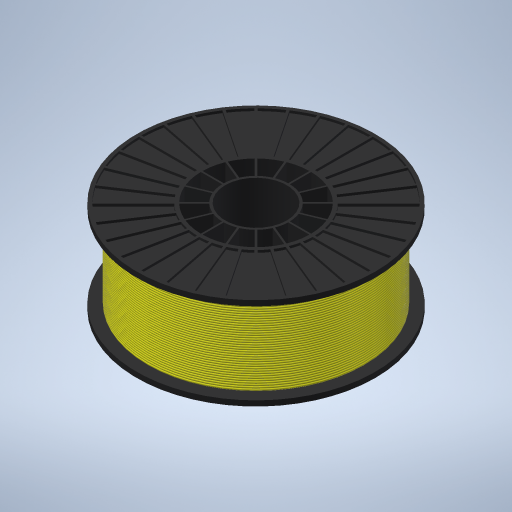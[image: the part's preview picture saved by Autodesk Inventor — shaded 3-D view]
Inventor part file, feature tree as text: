
AUTODESK INVENTOR PART (.ipt)
format: ipt  version: 2024 (Build 280153000, 153)  size: 1,131,008 bytes
history: native  units: mm
features: projected_geometry x10, extrude x7, pattern_circular x2, revolve x2, hole x1, mirror x1, pattern_linear x1
ambient origin geometry x8: Origin, YZ Plane, XZ Plane, XY Plane, X Axis, Y Axis, Z Axis, Center Point
bodies: Solid1 (feature_tree)
feature tree (24):
  extrude  "Extrusion1"  Depth=202.0mm
  hole  "Hole2"  [1 undecoded]
  extrude  "Extrusion3"  Depth=10.0mm
  extrude  "Extrusion4"  Depth=20.0mm
  pattern_circular  "Circular Pattern1"  [2 undecoded]
  extrude  "Extrusion5"  Depth=25.0mm TaperAngle=0.0deg
  extrude  "Extrusion6"  Depth=1.5mm
  pattern_circular  "Circular Pattern2"  [2 undecoded]
  mirror  "Mirror1"
  extrude  "Extrusion7"  Depth=160.0mm TaperAngle=360.0deg
  extrude  "Extrusion8"  Depth=3.0mm
  revolve  "Revolution1"  [1 undecoded]
  revolve  "Revolution2"  [1 undecoded]
  pattern_linear  "Rectangular Pattern1"  Spacing1=2.0mm  [1 undecoded]
  projected_geometry  "Projected Loop1"
  projected_geometry  "Projected Loop2"
  projected_geometry  "Projected Loop3"
  projected_geometry  "Projected Loop4"
  projected_geometry  "Projected Loop5"
  projected_geometry  "Projected Loop6"
  projected_geometry  "Projected Loop7"
  projected_geometry  "Project Cut Edges1"
  projected_geometry  "Project Cut Edges2"
  projected_geometry  "Project Cut Edges3"
note: 8 required parameter values undecoded (feature->parameter linkage not recoverable at this tier; creation-order binding heuristic only, values carry confidence <= 0.55)